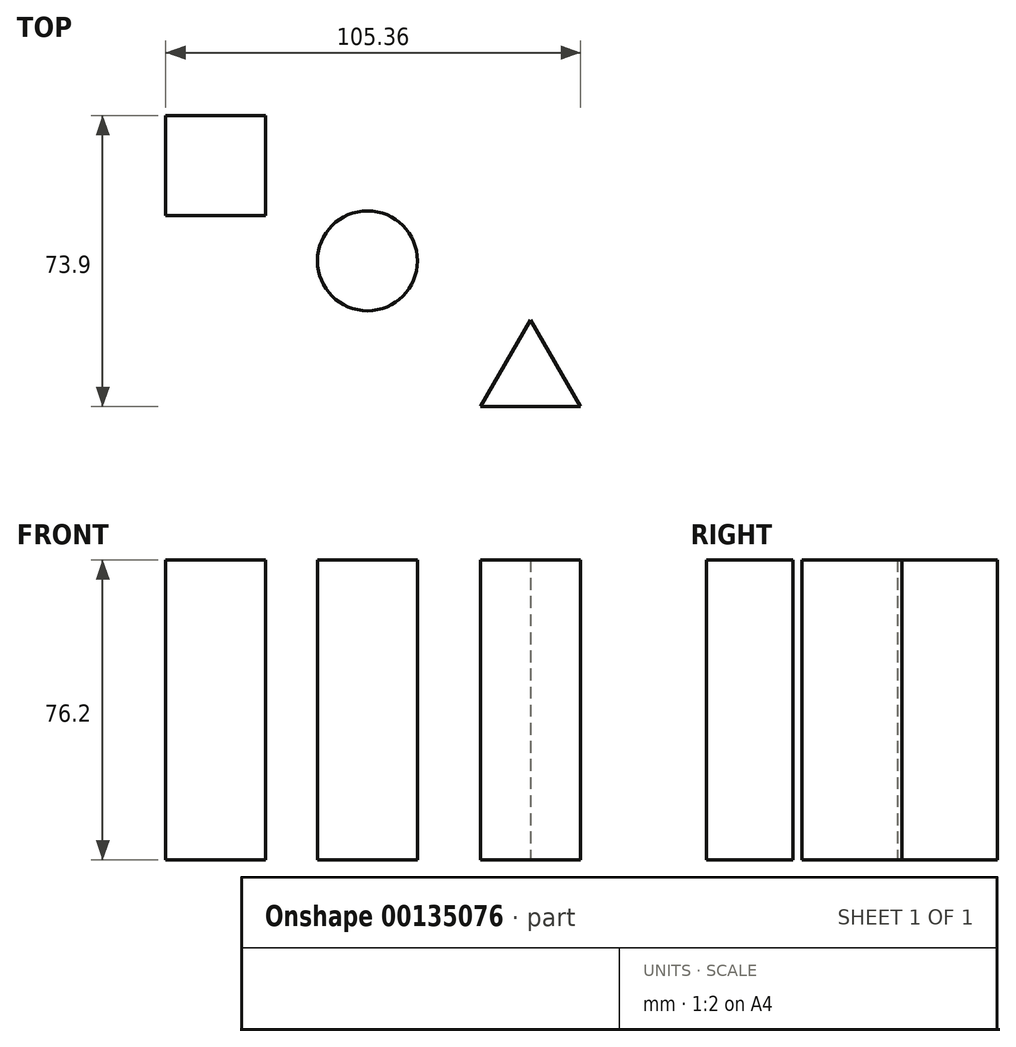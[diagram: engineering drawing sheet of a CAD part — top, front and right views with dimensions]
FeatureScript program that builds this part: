
annotation { "Feature Type Name" : "Feature", "Feature Type Description" : "" }
export const myFeature = defineFeature(function(context is Context, id is Id, definition is map)
    precondition{}
    {
        {
            var Q0;
            Q0=qCreatedBy(makeId("Top.planeOp"),FACE);
            var sketch = newSketch(context, id + "F0", { "sketchPlane" : qUnion([Q0])});
            skCircle(sketch, "E0", {"center": v(0, 0) * mm, "radius": 12.7 * mm});
            skSolve(sketch);
        }
        {
            var Q0;
            Q0=qCreatedBy(makeId("Top.planeOp"),FACE);
            var sketch = newSketch(context, id + "F1", { "sketchPlane" : qUnion([Q0])});
            skLineSegment(sketch, "E1.bottom", {"start": v(-51.26, 36.89) * mm, "end": v(-25.86, 36.89) * mm});
            skLineSegment(sketch, "E1.top", {"start": v(-51.26, 11.49) * mm, "end": v(-25.86, 11.49) * mm});
            skLineSegment(sketch, "E1.left", {"start": v(-51.26, 36.89) * mm, "end": v(-51.26, 11.49) * mm});
            skLineSegment(sketch, "E1.right", {"start": v(-25.86, 36.89) * mm, "end": v(-25.86, 11.49) * mm});
            skSolve(sketch);
        }
        {
            var Q0;
            Q0=makeQuery(id+"F0.imprint","IMPRINT",FACE,{"disambiguationData":[TD([[makeQuery(id+"F0.imprint","IMPRINT",EDGE,{"derivedFrom":sQuery(id+"F0.wireOp",EDGE,"E0")}),1.0]])]});
            extrude(context, id + "F2", {"entities" : qUnion([Q0]), "depth" : 76.2 * mm});
        }
        {
            var Q0;
            Q0=makeQuery(id+"F1.imprint","IMPRINT",FACE,{"disambiguationData":[TD([[makeQuery(id+"F1.imprint","IMPRINT",EDGE,{"derivedFrom":sQuery(id+"F1.wireOp",EDGE,"E1.bottom")}),-1.0]])]});
            var sketch = newSketch(context, id + "F3", { "sketchPlane" : qUnion([Q0])});
            skLineSegment(sketch, "E2", {"start": v(41.4, -15.02) * mm, "end": v(28.7, -37.01) * mm});
            skLineSegment(sketch, "E3", {"start": v(28.7, -37.01) * mm, "end": v(54.1, -37.01) * mm});
            skLineSegment(sketch, "E4", {"start": v(54.1, -37.01) * mm, "end": v(41.4, -15.02) * mm});
            skSolve(sketch);
        }
        {
            var Q0;
            Q0=makeQuery(id+"F1.imprint","IMPRINT",FACE,{"disambiguationData":[TD([[makeQuery(id+"F1.imprint","IMPRINT",EDGE,{"derivedFrom":sQuery(id+"F1.wireOp",EDGE,"E1.bottom")}),-1.0]])]});
            extrude(context, id + "F4", {"entities" : qUnion([Q0]), "depth" : 76.2 * mm});
        }
        {
            var Q0;
            Q0=makeQuery(id+"F3.imprint","IMPRINT",FACE,{"disambiguationData":[TD([[makeQuery(id+"F3.imprint","IMPRINT",EDGE,{"derivedFrom":sQuery(id+"F3.wireOp",EDGE,"E2")}),1.0]])]});
            extrude(context, id + "F5", {"entities" : qUnion([Q0]), "depth" : 76.2 * mm});
        }
    });
